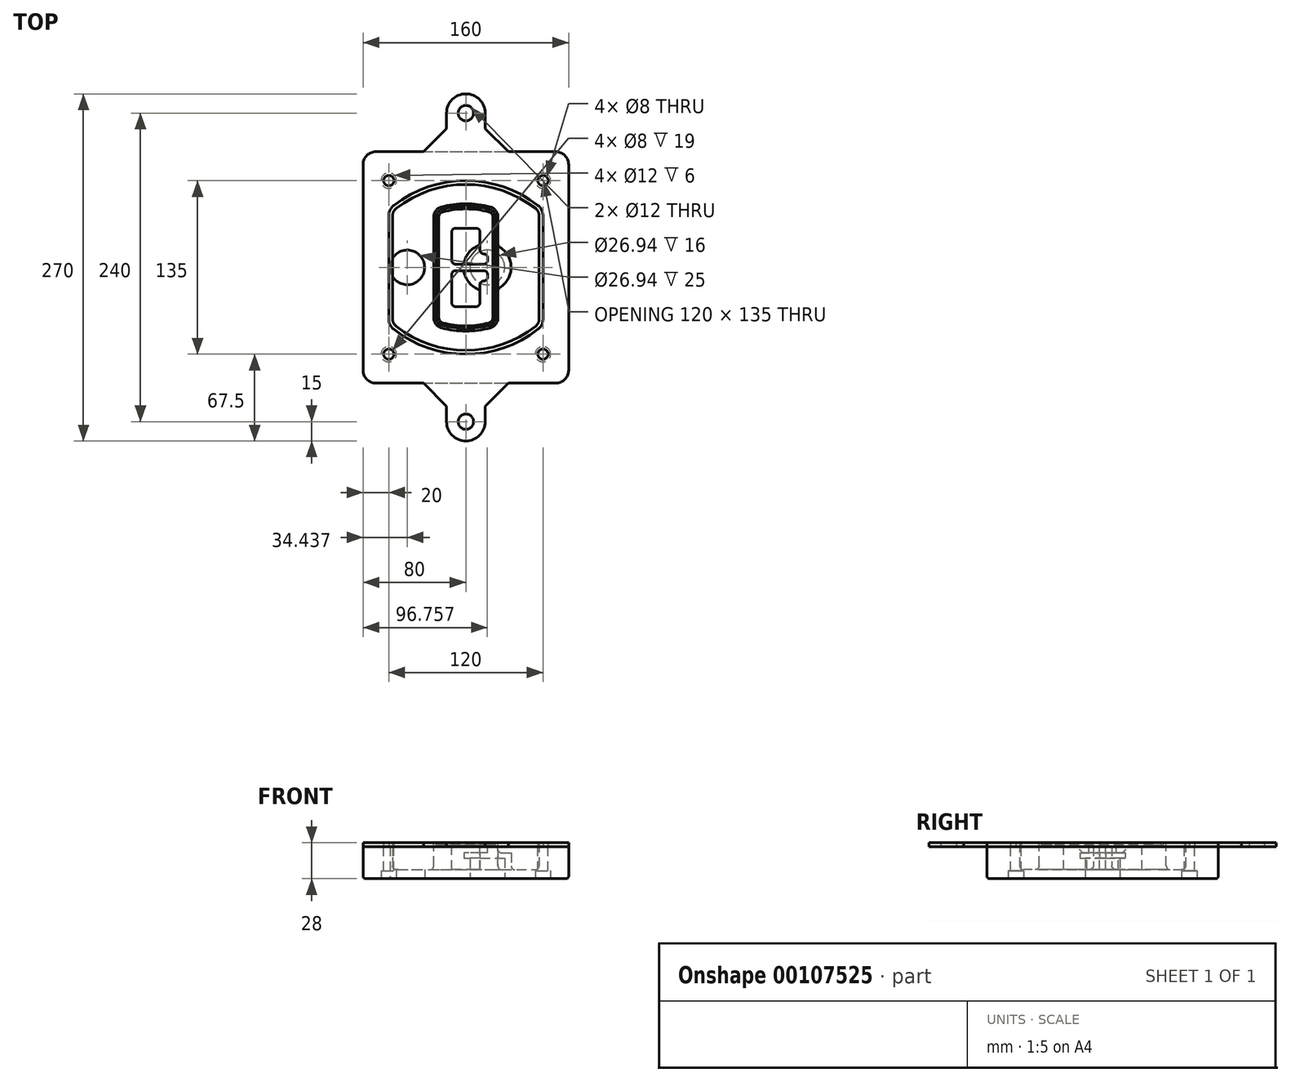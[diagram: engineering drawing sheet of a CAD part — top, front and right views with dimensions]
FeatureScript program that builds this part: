
annotation { "Feature Type Name" : "Feature", "Feature Type Description" : "" }
export const myFeature = defineFeature(function(context is Context, id is Id, definition is map)
    precondition{}
    {
        {
            var Q0;
            Q0=qCreatedBy(makeId("Top.planeOp"),FACE);
            var sketch = newSketch(context, id + "F0", { "sketchPlane" : qUnion([Q0])});
            skPoint(sketch, "E0.rect.middle", {"position": v(0, 0) * mm});
            skLineSegment(sketch, "E1.bottom", {"start": v(-70, -90) * mm, "end": v(70, -90) * mm});
            skLineSegment(sketch, "E1.top", {"start": v(-70, 90) * mm, "end": v(70, 90) * mm});
            skLineSegment(sketch, "E1.left", {"start": v(-80, -80) * mm, "end": v(-80, 80) * mm});
            skLineSegment(sketch, "E1.right", {"start": v(80, -80) * mm, "end": v(80, 80) * mm});
            skLineSegment(sketch, "E2", {"start": v(-80, 90) * mm, "end": v(80, -90) * mm, "construction": true});
            skLineSegment(sketch, "E3", {"start": v(80, 90) * mm, "end": v(-80, -90) * mm, "construction": true});
            skCircle(sketch, "E4", {"center": v(-60, 67.5) * mm, "radius": 4 * mm});
            skCircle(sketch, "E5", {"center": v(60, 67.5) * mm, "radius": 4 * mm});
            skCircle(sketch, "E6", {"center": v(60, -67.5) * mm, "radius": 4 * mm});
            skCircle(sketch, "E7", {"center": v(-60, -67.5) * mm, "radius": 4 * mm});
            skLineSegment(sketch, "E8", {"start": v(-60, 67.5) * mm, "end": v(60, 67.5) * mm, "construction": true});
            skLineSegment(sketch, "E9", {"start": v(60, 67.5) * mm, "end": v(60, -67.5) * mm, "construction": true});
            skLineSegment(sketch, "E10", {"start": v(60, -67.5) * mm, "end": v(-60, -67.5) * mm, "construction": true});
            skLineSegment(sketch, "E11", {"start": v(-60, -67.5) * mm, "end": v(-60, 67.5) * mm, "construction": true});
            skLineSegment(sketch, "E12", {"start": v(-60, 40.3) * mm, "end": v(-60, -40.3) * mm});
            skLineSegment(sketch, "E13", {"start": v(60, 40.3) * mm, "end": v(60, -40.3) * mm});
            skArc(sketch, "E14", {"start": v(56.15, 48.18) * mm, "mid": v(0, 67.5) * mm, "end": v(-56.15, 48.18) * mm});
            skArc(sketch, "E15", {"start": v(-56.15, -48.18) * mm, "mid": v(0, -67.5) * mm, "end": v(56.15, -48.18) * mm});
            skLineSegment(sketch, "E16", {"start": v(-60, 0) * mm, "end": v(60, 0) * mm, "construction": true});
            skPoint(sketch, "E17.visualSharp", {"position": v(-60, -45) * mm});
            skArc(sketch, "E17.filletArc", {"start": v(-60, -40.3) * mm, "mid": v(-58.99, -44.68) * mm, "end": v(-56.15, -48.18) * mm});
            skPoint(sketch, "E18.visualSharp", {"position": v(-60, 45) * mm});
            skArc(sketch, "E18.filletArc", {"start": v(-56.15, 48.18) * mm, "mid": v(-58.99, 44.68) * mm, "end": v(-60, 40.3) * mm});
            skPoint(sketch, "E19.visualSharp", {"position": v(60, 45) * mm});
            skArc(sketch, "E19.filletArc", {"start": v(60, 40.3) * mm, "mid": v(58.99, 44.68) * mm, "end": v(56.15, 48.18) * mm});
            skPoint(sketch, "E20.visualSharp", {"position": v(60, -45) * mm});
            skArc(sketch, "E20.filletArc", {"start": v(56.15, -48.18) * mm, "mid": v(58.99, -44.68) * mm, "end": v(60, -40.3) * mm});
            skPoint(sketch, "E21.visualSharp", {"position": v(-80, 90) * mm});
            skArc(sketch, "E21.filletArc", {"start": v(-70, 90) * mm, "mid": v(-77.07, 87.07) * mm, "end": v(-80, 80) * mm});
            skPoint(sketch, "E22.visualSharp", {"position": v(80, 90) * mm});
            skArc(sketch, "E22.filletArc", {"start": v(80, 80) * mm, "mid": v(77.07, 87.07) * mm, "end": v(70, 90) * mm});
            skPoint(sketch, "E23.visualSharp", {"position": v(80, -90) * mm});
            skArc(sketch, "E23.filletArc", {"start": v(70, -90) * mm, "mid": v(77.07, -87.07) * mm, "end": v(80, -80) * mm});
            skPoint(sketch, "E24.visualSharp", {"position": v(-80, -90) * mm});
            skArc(sketch, "E24.filletArc", {"start": v(-80, -80) * mm, "mid": v(-77.07, -87.07) * mm, "end": v(-70, -90) * mm});
            skArc(sketch, "E25.0", {"start": v(57, 40.3) * mm, "mid": v(56.3, 43.36) * mm, "end": v(54.3, 45.81) * mm});
            skLineSegment(sketch, "E25.1", {"start": v(57, 40.3) * mm, "end": v(57, -40.3) * mm});
            skArc(sketch, "E25.2", {"start": v(54.3, -45.81) * mm, "mid": v(56.3, -43.36) * mm, "end": v(57, -40.3) * mm});
            skArc(sketch, "E25.3", {"start": v(-54.3, -45.81) * mm, "mid": v(0, -64.5) * mm, "end": v(54.3, -45.81) * mm});
            skArc(sketch, "E25.4", {"start": v(-57, -40.3) * mm, "mid": v(-56.3, -43.36) * mm, "end": v(-54.3, -45.81) * mm});
            skArc(sketch, "E25.5", {"start": v(54.3, 45.81) * mm, "mid": v(0, 64.5) * mm, "end": v(-54.3, 45.81) * mm});
            skLineSegment(sketch, "E25.6", {"start": v(-57, 40.3) * mm, "end": v(-57, -40.3) * mm});
            skArc(sketch, "E25.7", {"start": v(-54.3, 45.81) * mm, "mid": v(-56.3, 43.36) * mm, "end": v(-57, 40.3) * mm});
            skArc(sketch, "E26.0", {"start": v(-58.62, 51.33) * mm, "mid": v(-62.58, 46.43) * mm, "end": v(-64, 40.3) * mm});
            skArc(sketch, "E26.1", {"start": v(58.62, 51.33) * mm, "mid": v(0, 71.5) * mm, "end": v(-58.62, 51.33) * mm});
            skArc(sketch, "E26.2", {"start": v(64, 40.3) * mm, "mid": v(62.58, 46.43) * mm, "end": v(58.62, 51.33) * mm});
            skLineSegment(sketch, "E26.3", {"start": v(64, 40.3) * mm, "end": v(64, -40.3) * mm});
            skArc(sketch, "E26.4", {"start": v(58.62, -51.33) * mm, "mid": v(62.58, -46.43) * mm, "end": v(64, -40.3) * mm});
            skLineSegment(sketch, "E26.5", {"start": v(-64, 40.3) * mm, "end": v(-64, -40.3) * mm});
            skArc(sketch, "E26.6", {"start": v(-58.62, -51.33) * mm, "mid": v(0, -71.5) * mm, "end": v(58.62, -51.33) * mm});
            skArc(sketch, "E26.7", {"start": v(-64, -40.3) * mm, "mid": v(-62.58, -46.43) * mm, "end": v(-58.62, -51.33) * mm});
            skSolve(sketch);
        }
        {
            var Q0;
            Q0=makeQuery(id+"F0.imprint","IMPRINT",FACE,{"disambiguationData":[TD([[makeQuery(id+"F0.imprint","IMPRINT",EDGE,{"derivedFrom":sQuery(id+"F0.wireOp",EDGE,"E1.bottom")}),1.0]])]});
            var Q1;
            Q1=makeQuery(id+"F0.imprint","IMPRINT",FACE,{"disambiguationData":[TD([[makeQuery(id+"F0.imprint","IMPRINT",EDGE,{"derivedFrom":sQuery(id+"F0.wireOp",EDGE,"E12")}),1.0]])]});
            var Q2;
            Q2=makeQuery(id+"F0.imprint","IMPRINT",FACE,{"disambiguationData":[TD([[makeQuery(id+"F0.imprint","IMPRINT",EDGE,{"derivedFrom":sQuery(id+"F0.wireOp",EDGE,"E25.0")}),1.0]])]});
            var Q3;
            Q3=makeQuery(id+"F0.imprint","IMPRINT",FACE,{"disambiguationData":[TD([[makeQuery(id+"F0.imprint","IMPRINT",EDGE,{"derivedFrom":sQuery(id+"F0.wireOp",EDGE,"E12")}),-1.0]])]});
            extrude(context, id + "F1", {"entities" : qUnion([Q0, Q1, Q2, Q3]), "oppositeDirection" : true, "depth" : 25 * mm});
        }
        {
            var Q0;
            Q0=makeQuery(id+"F0.imprint","IMPRINT",FACE,{"disambiguationData":[TD([[makeQuery(id+"F0.imprint","IMPRINT",EDGE,{"derivedFrom":sQuery(id+"F0.wireOp",EDGE,"E12")}),1.0]])]});
            extrude(context, id + "F2", {"entities" : qUnion([Q0]), "operationType" : NewBodyOperationType.ADD, "depth" : 3 * mm});
        }
        {
            var Q0;
            Q0=makeQuery(id+"F0.imprint","IMPRINT",FACE,{"disambiguationData":[TD([[makeQuery(id+"F0.imprint","IMPRINT",EDGE,{"derivedFrom":sQuery(id+"F0.wireOp",EDGE,"E25.0")}),1.0]])]});
            extrude(context, id + "F3", {"entities" : qUnion([Q0]), "operationType" : NewBodyOperationType.REMOVE, "oppositeDirection" : true, "depth" : 18 * mm});
        }
        {
            var Q0;
            Q0=makeQuery(id+"F2.opExtrude","CAP_FACE",FACE,{"disambiguationData":[OSD([sQuery(id+"F0.wireOp",EDGE,"E12"),sQuery(id+"F0.wireOp",EDGE,"E13"),sQuery(id+"F0.wireOp",EDGE,"E14"),sQuery(id+"F0.wireOp",EDGE,"E15"),sQuery(id+"F0.wireOp",EDGE,"E17.filletArc"),sQuery(id+"F0.wireOp",EDGE,"E18.filletArc"),sQuery(id+"F0.wireOp",EDGE,"E19.filletArc"),sQuery(id+"F0.wireOp",EDGE,"E20.filletArc"),sQuery(id+"F0.wireOp",EDGE,"E25.0"),sQuery(id+"F0.wireOp",EDGE,"E25.1"),sQuery(id+"F0.wireOp",EDGE,"E25.2"),sQuery(id+"F0.wireOp",EDGE,"E25.3"),sQuery(id+"F0.wireOp",EDGE,"E25.4"),sQuery(id+"F0.wireOp",EDGE,"E25.5"),sQuery(id+"F0.wireOp",EDGE,"E25.6"),sQuery(id+"F0.wireOp",EDGE,"E25.7")])],"isStart":false});
            var sketch = newSketch(context, id + "F4", { "sketchPlane" : qUnion([Q0])});
            skArc(sketch, "E27.0", {"start": v(-19.08, -46.97) * mm, "mid": v(0, -49.5) * mm, "end": v(19.08, -46.97) * mm});
            skArc(sketch, "E28.0", {"start": v(19.08, 46.97) * mm, "mid": v(0, 49.5) * mm, "end": v(-19.08, 46.97) * mm});
            skLineSegment(sketch, "E29", {"start": v(-25, 39.25) * mm, "end": v(-25, -39.25) * mm});
            skLineSegment(sketch, "E30", {"start": v(25, 39.25) * mm, "end": v(25, -39.25) * mm});
            skLineSegment(sketch, "E31", {"start": v(-25, 45.1) * mm, "end": v(25, 45.1) * mm, "construction": true});
            skLineSegment(sketch, "E32", {"start": v(-25, -45.1) * mm, "end": v(25, -45.1) * mm, "construction": true});
            skPoint(sketch, "E33.visualSharp", {"position": v(-25, 45.1) * mm});
            skArc(sketch, "E33.filletArc", {"start": v(-19.08, 46.97) * mm, "mid": v(-23.35, 44.11) * mm, "end": v(-25, 39.25) * mm});
            skPoint(sketch, "E34.visualSharp", {"position": v(25, 45.1) * mm});
            skArc(sketch, "E34.filletArc", {"start": v(25, 39.25) * mm, "mid": v(23.35, 44.11) * mm, "end": v(19.08, 46.97) * mm});
            skPoint(sketch, "E35.visualSharp", {"position": v(25, -45.1) * mm});
            skArc(sketch, "E35.filletArc", {"start": v(19.08, -46.97) * mm, "mid": v(23.35, -44.11) * mm, "end": v(25, -39.25) * mm});
            skPoint(sketch, "E36.visualSharp", {"position": v(-25, -45.1) * mm});
            skArc(sketch, "E36.filletArc", {"start": v(-25, -39.25) * mm, "mid": v(-23.35, -44.11) * mm, "end": v(-19.08, -46.97) * mm});
            skArc(sketch, "E37.0", {"start": v(54.3, 45.81) * mm, "mid": v(0, 64.5) * mm, "end": v(-54.3, 45.81) * mm});
            skArc(sketch, "E37.1", {"start": v(-54.3, 45.81) * mm, "mid": v(-56.3, 43.36) * mm, "end": v(-57, 40.3) * mm});
            skLineSegment(sketch, "E37.2", {"start": v(-57, 40.3) * mm, "end": v(-57, -40.3) * mm});
            skArc(sketch, "E37.3", {"start": v(-57, -40.3) * mm, "mid": v(-56.3, -43.36) * mm, "end": v(-54.3, -45.81) * mm});
            skArc(sketch, "E37.4", {"start": v(-54.3, -45.81) * mm, "mid": v(0, -64.5) * mm, "end": v(54.3, -45.81) * mm});
            skArc(sketch, "E37.5", {"start": v(54.3, -45.81) * mm, "mid": v(56.3, -43.36) * mm, "end": v(57, -40.3) * mm});
            skLineSegment(sketch, "E37.6", {"start": v(57, 40.3) * mm, "end": v(57, -40.3) * mm});
            skArc(sketch, "E37.7", {"start": v(57, 40.3) * mm, "mid": v(56.3, 43.36) * mm, "end": v(54.3, 45.81) * mm});
            skLineSegment(sketch, "E38.0", {"start": v(23, 39.25) * mm, "end": v(23, -39.25) * mm});
            skArc(sketch, "E38.1", {"start": v(18.56, -45.04) * mm, "mid": v(21.76, -42.9) * mm, "end": v(23, -39.25) * mm});
            skArc(sketch, "E38.2", {"start": v(-18.56, -45.04) * mm, "mid": v(0, -47.5) * mm, "end": v(18.56, -45.04) * mm});
            skArc(sketch, "E38.3", {"start": v(-23, -39.25) * mm, "mid": v(-21.76, -42.9) * mm, "end": v(-18.56, -45.04) * mm});
            skLineSegment(sketch, "E38.4", {"start": v(-23, 39.25) * mm, "end": v(-23, -39.25) * mm});
            skArc(sketch, "E38.5", {"start": v(23, 39.25) * mm, "mid": v(21.76, 42.9) * mm, "end": v(18.56, 45.04) * mm});
            skArc(sketch, "E38.6", {"start": v(-18.56, 45.04) * mm, "mid": v(-21.76, 42.9) * mm, "end": v(-23, 39.25) * mm});
            skArc(sketch, "E38.7", {"start": v(18.56, 45.04) * mm, "mid": v(0, 47.5) * mm, "end": v(-18.56, 45.04) * mm});
            skArc(sketch, "E39.0", {"start": v(21, 39.25) * mm, "mid": v(20.18, 41.68) * mm, "end": v(18.04, 43.1) * mm});
            skLineSegment(sketch, "E39.1", {"start": v(21, 39.25) * mm, "end": v(21, -39.25) * mm});
            skArc(sketch, "E39.2", {"start": v(18.04, -43.1) * mm, "mid": v(20.18, -41.68) * mm, "end": v(21, -39.25) * mm});
            skArc(sketch, "E39.3", {"start": v(-18.04, -43.1) * mm, "mid": v(0, -45.5) * mm, "end": v(18.04, -43.1) * mm});
            skArc(sketch, "E39.4", {"start": v(-21, -39.25) * mm, "mid": v(-20.18, -41.68) * mm, "end": v(-18.04, -43.1) * mm});
            skArc(sketch, "E39.5", {"start": v(18.04, 43.1) * mm, "mid": v(0, 45.5) * mm, "end": v(-18.04, 43.1) * mm});
            skLineSegment(sketch, "E39.6", {"start": v(-21, 39.25) * mm, "end": v(-21, -39.25) * mm});
            skArc(sketch, "E39.7", {"start": v(-18.04, 43.1) * mm, "mid": v(-20.18, 41.68) * mm, "end": v(-21, 39.25) * mm});
            skLineSegment(sketch, "E40", {"start": v(-25, 0) * mm, "end": v(25, 0) * mm, "construction": true});
            skLineSegment(sketch, "E41", {"start": v(-11, 5.5) * mm, "end": v(-11, 27.5) * mm});
            skLineSegment(sketch, "E42", {"start": v(-8, 30.5) * mm, "end": v(8, 30.5) * mm});
            skLineSegment(sketch, "E43", {"start": v(11, 27.5) * mm, "end": v(11, 13.5) * mm});
            skLineSegment(sketch, "E44", {"start": v(14, 10.5) * mm, "end": v(14, 10.5) * mm});
            skLineSegment(sketch, "E45", {"start": v(17, 7.5) * mm, "end": v(17, 5.5) * mm});
            skLineSegment(sketch, "E46", {"start": v(14, 2.5) * mm, "end": v(-8, 2.5) * mm});
            skPoint(sketch, "E47.visualSharp", {"position": v(-11, 30.5) * mm});
            skArc(sketch, "E47.filletArc", {"start": v(-8, 30.5) * mm, "mid": v(-10.12, 29.62) * mm, "end": v(-11, 27.5) * mm});
            skPoint(sketch, "E48.visualSharp", {"position": v(11, 30.5) * mm});
            skArc(sketch, "E48.filletArc", {"start": v(11, 27.5) * mm, "mid": v(10.12, 29.62) * mm, "end": v(8, 30.5) * mm});
            skPoint(sketch, "E49.visualSharp", {"position": v(11, 10.5) * mm});
            skArc(sketch, "E49.filletArc", {"start": v(11, 13.5) * mm, "mid": v(11.88, 11.38) * mm, "end": v(14, 10.5) * mm});
            skPoint(sketch, "E50.visualSharp", {"position": v(17, 10.5) * mm});
            skArc(sketch, "E50.filletArc", {"start": v(17, 7.5) * mm, "mid": v(16.12, 9.62) * mm, "end": v(14, 10.5) * mm});
            skPoint(sketch, "E51.visualSharp", {"position": v(17, 2.5) * mm});
            skArc(sketch, "E51.filletArc", {"start": v(14, 2.5) * mm, "mid": v(16.12, 3.38) * mm, "end": v(17, 5.5) * mm});
            skPoint(sketch, "E52.visualSharp", {"position": v(-11, 2.5) * mm});
            skArc(sketch, "E52.filletArc", {"start": v(-11, 5.5) * mm, "mid": v(-10.12, 3.38) * mm, "end": v(-8, 2.5) * mm});
            skLineSegment(sketch, "E53.0.MirrorCS", {"start": v(14, -2.5) * mm, "end": v(-8, -2.5) * mm});
            skArc(sketch, "E54.0.MirrorCS", {"start": v(-11, -5.5) * mm, "mid": v(-10.12, -3.38) * mm, "end": v(-8, -2.5) * mm});
            skLineSegment(sketch, "E55.0.MirrorCS", {"start": v(-11, -5.5) * mm, "end": v(-11, -27.5) * mm});
            skArc(sketch, "E56.0.MirrorCS", {"start": v(-8, -30.5) * mm, "mid": v(-10.12, -29.62) * mm, "end": v(-11, -27.5) * mm});
            skLineSegment(sketch, "E57.0.MirrorCS", {"start": v(-8, -30.5) * mm, "end": v(8, -30.5) * mm});
            skArc(sketch, "E58.0.MirrorCS", {"start": v(11, -27.5) * mm, "mid": v(10.12, -29.62) * mm, "end": v(8, -30.5) * mm});
            skLineSegment(sketch, "E59.0.MirrorCS", {"start": v(11, -27.5) * mm, "end": v(11, -13.5) * mm});
            skArc(sketch, "E60.0.MirrorCS", {"start": v(11, -13.5) * mm, "mid": v(11.88, -11.38) * mm, "end": v(14, -10.5) * mm});
            skArc(sketch, "E61.0.MirrorCS", {"start": v(17, -7.5) * mm, "mid": v(16.12, -9.62) * mm, "end": v(14, -10.5) * mm});
            skLineSegment(sketch, "E62.0.MirrorCS", {"start": v(17, -7.5) * mm, "end": v(17, -5.5) * mm});
            skArc(sketch, "E63.0.MirrorCS", {"start": v(14, -2.5) * mm, "mid": v(16.12, -3.38) * mm, "end": v(17, -5.5) * mm});
            skSolve(sketch);
        }
        {
            var Q0;
            Q0=makeQuery(id+"F4.imprint","IMPRINT",FACE,{"disambiguationData":[TD([[makeQuery(id+"F4.imprint","IMPRINT",EDGE,{"derivedFrom":sQuery(id+"F4.wireOp",EDGE,"E27.0")}),1.0]])]});
            var Q1;
            Q1=makeQuery(id+"F4.imprint","IMPRINT",FACE,{"disambiguationData":[TD([[makeQuery(id+"F4.imprint","IMPRINT",EDGE,{"derivedFrom":sQuery(id+"F4.wireOp",EDGE,"E38.0")}),-1.0]])]});
            var Q2;
            Q2=makeQuery(id+"F4.imprint","IMPRINT",FACE,{"disambiguationData":[TD([[makeQuery(id+"F4.imprint","IMPRINT",EDGE,{"derivedFrom":sQuery(id+"F4.wireOp",EDGE,"E39.0")}),1.0]])]});
            extrude(context, id + "F5", {"entities" : qUnion([Q0, Q1, Q2]), "operationType" : NewBodyOperationType.ADD, "endBound" : BoundingType.UP_TO_NEXT, "oppositeDirection" : true, "depth" : 25 * mm});
        }
        {
            var Q0;
            Q0=makeQuery(id+"F4.imprint","IMPRINT",FACE,{"disambiguationData":[TD([[makeQuery(id+"F4.imprint","IMPRINT",EDGE,{"derivedFrom":sQuery(id+"F4.wireOp",EDGE,"E38.0")}),-1.0]])]});
            extrude(context, id + "F6", {"entities" : qUnion([Q0]), "operationType" : NewBodyOperationType.REMOVE, "oppositeDirection" : true, "depth" : 2 * mm});
        }
        {
            var Q0;
            Q0=makeQuery(id+"F1.opExtrude","CAP_FACE",FACE,{"disambiguationData":[OSD([sQuery(id+"F0.wireOp",EDGE,"E1.bottom"),sQuery(id+"F0.wireOp",EDGE,"E1.top"),sQuery(id+"F0.wireOp",EDGE,"E1.left"),sQuery(id+"F0.wireOp",EDGE,"E1.right"),sQuery(id+"F0.wireOp",EDGE,"E4"),sQuery(id+"F0.wireOp",EDGE,"E5"),sQuery(id+"F0.wireOp",EDGE,"E6"),sQuery(id+"F0.wireOp",EDGE,"E7"),sQuery(id+"F0.wireOp",EDGE,"E21.filletArc"),sQuery(id+"F0.wireOp",EDGE,"E22.filletArc"),sQuery(id+"F0.wireOp",EDGE,"E23.filletArc"),sQuery(id+"F0.wireOp",EDGE,"E24.filletArc")])],"isStart":false});
            var sketch = newSketch(context, id + "F7", { "sketchPlane" : qUnion([Q0])});
            skCircle(sketch, "E64", {"center": v(16.76, 0) * mm, "radius": 13.47 * mm});
            skCircle(sketch, "E65", {"center": v(-45.56, 0) * mm, "radius": 13.47 * mm});
            skLineSegment(sketch, "E66", {"start": v(80, 0) * mm, "end": v(-80, 0) * mm});
            skCircle(sketch, "E67", {"center": v(16.76, 0) * mm, "radius": 18.47 * mm});
            skCircle(sketch, "E68", {"center": v(60, -67.5) * mm, "radius": 6 * mm});
            skCircle(sketch, "E69", {"center": v(-60, -67.5) * mm, "radius": 6 * mm});
            skCircle(sketch, "E70", {"center": v(-60, 67.5) * mm, "radius": 6 * mm});
            skCircle(sketch, "E71", {"center": v(60, 67.5) * mm, "radius": 6 * mm});
            skSolve(sketch);
        }
        {
            var Q0;
            {var subQ1=sQuery(id+"F7.wireOp",EDGE,"E66");var subQ4=sQuery(id+"F7.wireOp",EDGE,"E64");var subQ6=makeQuery(id+"F7.imprint","INTERSECT",VERTEX,{"disambiguationData":[OD(0.0)],"derivedFrom":[subQ4,subQ1]});Q0=makeQuery(id+"F7.imprint","IMPRINT",FACE,{"disambiguationData":[TD([[makeQuery(id+"F7.imprint","IMPRINT",EDGE,{"disambiguationData":[TD([[subQ6,-1.0]])],"derivedFrom":subQ4}),-1.0]])]});}
            var Q1;
            {var subQ0=sQuery(id+"F7.wireOp",EDGE,"E66");var subQ1=sQuery(id+"F7.wireOp",EDGE,"E64");var subQ3=makeQuery(id+"F7.imprint","INTERSECT",VERTEX,{"disambiguationData":[OD(0.0)],"derivedFrom":[subQ1,subQ0]});Q1=makeQuery(id+"F7.imprint","IMPRINT",FACE,{"disambiguationData":[TD([[makeQuery(id+"F7.imprint","IMPRINT",EDGE,{"disambiguationData":[TD([[subQ3,-1.0]])],"derivedFrom":subQ1}),1.0]])]});}
            var Q2;
            {var subQ0=sQuery(id+"F7.wireOp",EDGE,"E66");var subQ1=sQuery(id+"F7.wireOp",EDGE,"E64");var subQ3=makeQuery(id+"F7.imprint","INTERSECT",VERTEX,{"disambiguationData":[OD(0.0)],"derivedFrom":[subQ1,subQ0]});Q2=makeQuery(id+"F7.imprint","IMPRINT",FACE,{"disambiguationData":[TD([[makeQuery(id+"F7.imprint","IMPRINT",EDGE,{"disambiguationData":[TD([[subQ3,1.0]])],"derivedFrom":subQ1}),1.0]])]});}
            var Q3;
            {var subQ1=sQuery(id+"F7.wireOp",EDGE,"E66");var subQ4=sQuery(id+"F7.wireOp",EDGE,"E64");var subQ6=makeQuery(id+"F7.imprint","INTERSECT",VERTEX,{"disambiguationData":[OD(0.0)],"derivedFrom":[subQ4,subQ1]});Q3=makeQuery(id+"F7.imprint","IMPRINT",FACE,{"disambiguationData":[TD([[makeQuery(id+"F7.imprint","IMPRINT",EDGE,{"disambiguationData":[TD([[subQ6,1.0]])],"derivedFrom":subQ4}),-1.0]])]});}
            extrude(context, id + "F8", {"entities" : qUnion([Q0, Q1, Q2, Q3]), "operationType" : NewBodyOperationType.ADD, "oppositeDirection" : true, "depth" : 20 * mm});
        }
        {
            var Q0;
            {var subQ0=sQuery(id+"F7.wireOp",EDGE,"E66");var subQ1=sQuery(id+"F7.wireOp",EDGE,"E64");var subQ3=makeQuery(id+"F7.imprint","INTERSECT",VERTEX,{"disambiguationData":[OD(0.0)],"derivedFrom":[subQ1,subQ0]});Q0=makeQuery(id+"F7.imprint","IMPRINT",FACE,{"disambiguationData":[TD([[makeQuery(id+"F7.imprint","IMPRINT",EDGE,{"disambiguationData":[TD([[subQ3,-1.0]])],"derivedFrom":subQ1}),1.0]])]});}
            var Q1;
            {var subQ0=sQuery(id+"F7.wireOp",EDGE,"E66");var subQ1=sQuery(id+"F7.wireOp",EDGE,"E64");var subQ3=makeQuery(id+"F7.imprint","INTERSECT",VERTEX,{"disambiguationData":[OD(0.0)],"derivedFrom":[subQ1,subQ0]});Q1=makeQuery(id+"F7.imprint","IMPRINT",FACE,{"disambiguationData":[TD([[makeQuery(id+"F7.imprint","IMPRINT",EDGE,{"disambiguationData":[TD([[subQ3,1.0]])],"derivedFrom":subQ1}),1.0]])]});}
            extrude(context, id + "F9", {"entities" : qUnion([Q0, Q1]), "operationType" : NewBodyOperationType.REMOVE, "oppositeDirection" : true, "depth" : 16 * mm});
        }
        {
            var Q0;
            {var subQ0=sQuery(id+"F7.wireOp",EDGE,"E66");var subQ1=sQuery(id+"F7.wireOp",EDGE,"E65");var subQ3=makeQuery(id+"F7.imprint","INTERSECT",VERTEX,{"disambiguationData":[OD(0.0)],"derivedFrom":[subQ1,subQ0]});Q0=makeQuery(id+"F7.imprint","IMPRINT",FACE,{"disambiguationData":[TD([[makeQuery(id+"F7.imprint","IMPRINT",EDGE,{"disambiguationData":[TD([[subQ3,-1.0]])],"derivedFrom":subQ1}),1.0]])]});}
            var Q1;
            {var subQ0=sQuery(id+"F7.wireOp",EDGE,"E66");var subQ1=sQuery(id+"F7.wireOp",EDGE,"E65");var subQ3=makeQuery(id+"F7.imprint","INTERSECT",VERTEX,{"disambiguationData":[OD(0.0)],"derivedFrom":[subQ1,subQ0]});Q1=makeQuery(id+"F7.imprint","IMPRINT",FACE,{"disambiguationData":[TD([[makeQuery(id+"F7.imprint","IMPRINT",EDGE,{"disambiguationData":[TD([[subQ3,1.0]])],"derivedFrom":subQ1}),1.0]])]});}
            extrude(context, id + "F10", {"entities" : qUnion([Q0, Q1]), "operationType" : NewBodyOperationType.REMOVE, "oppositeDirection" : true, "depth" : 25 * mm});
        }
        {
            var Q0;
            Q0=makeQuery(id+"F7.imprint","IMPRINT",FACE,{"disambiguationData":[TD([[makeQuery(id+"F7.imprint","IMPRINT",EDGE,{"derivedFrom":sQuery(id+"F7.wireOp",EDGE,"E68")}),1.0]])]});
            var Q1;
            Q1=makeQuery(id+"F7.imprint","IMPRINT",FACE,{"disambiguationData":[TD([[makeQuery(id+"F7.imprint","IMPRINT",EDGE,{"derivedFrom":makeQuery(id+"F1.opExtrude","CAP_EDGE",EDGE,{"disambiguationData":[OSD([sQuery(id+"F0.wireOp",EDGE,"E5")])],"isStart":false})}),-1.0]])]});
            var Q2;
            Q2=makeQuery(id+"F7.imprint","IMPRINT",FACE,{"disambiguationData":[TD([[makeQuery(id+"F7.imprint","IMPRINT",EDGE,{"derivedFrom":sQuery(id+"F7.wireOp",EDGE,"E69")}),1.0]])]});
            var Q3;
            Q3=makeQuery(id+"F7.imprint","IMPRINT",FACE,{"disambiguationData":[TD([[makeQuery(id+"F7.imprint","IMPRINT",EDGE,{"derivedFrom":makeQuery(id+"F1.opExtrude","CAP_EDGE",EDGE,{"disambiguationData":[OSD([sQuery(id+"F0.wireOp",EDGE,"E4")])],"isStart":false})}),-1.0]])]});
            var Q4;
            Q4=makeQuery(id+"F7.imprint","IMPRINT",FACE,{"disambiguationData":[TD([[makeQuery(id+"F7.imprint","IMPRINT",EDGE,{"derivedFrom":sQuery(id+"F7.wireOp",EDGE,"E70")}),1.0]])]});
            var Q5;
            Q5=makeQuery(id+"F7.imprint","IMPRINT",FACE,{"disambiguationData":[TD([[makeQuery(id+"F7.imprint","IMPRINT",EDGE,{"derivedFrom":makeQuery(id+"F1.opExtrude","CAP_EDGE",EDGE,{"disambiguationData":[OSD([sQuery(id+"F0.wireOp",EDGE,"E7")])],"isStart":false})}),-1.0]])]});
            var Q6;
            Q6=makeQuery(id+"F7.imprint","IMPRINT",FACE,{"disambiguationData":[TD([[makeQuery(id+"F7.imprint","IMPRINT",EDGE,{"derivedFrom":sQuery(id+"F7.wireOp",EDGE,"E71")}),1.0]])]});
            var Q7;
            Q7=makeQuery(id+"F7.imprint","IMPRINT",FACE,{"disambiguationData":[TD([[makeQuery(id+"F7.imprint","IMPRINT",EDGE,{"derivedFrom":makeQuery(id+"F1.opExtrude","CAP_EDGE",EDGE,{"disambiguationData":[OSD([sQuery(id+"F0.wireOp",EDGE,"E6")])],"isStart":false})}),-1.0]])]});
            extrude(context, id + "F11", {"entities" : qUnion([Q0, Q1, Q2, Q3, Q4, Q5, Q6, Q7]), "operationType" : NewBodyOperationType.REMOVE, "oppositeDirection" : true, "depth" : 6 * mm});
        }
        {
            var Q0;
            Q0=makeQuery(id+"F9.boolean.opBoolean","COPY",FACE,{"derivedFrom":makeQuery(id+"F9.opExtrude","CAP_FACE",FACE,{"disambiguationData":[OSD([sQuery(id+"F7.wireOp",EDGE,"E64")])],"isStart":false})});
            var sketch = newSketch(context, id + "F12", { "sketchPlane" : qUnion([Q0])});
            skArc(sketch, "E72.0", {"start": v(11, 17.55) * mm, "mid": v(2.57, 11.82) * mm, "end": v(-1.54, 2.5) * mm});
            skArc(sketch, "E72.1", {"start": v(-1.54, -2.5) * mm, "mid": v(2.57, -11.82) * mm, "end": v(11, -17.55) * mm});
            skLineSegment(sketch, "E73", {"start": v(-1.54, -2.5) * mm, "end": v(14, -2.5) * mm});
            skLineSegment(sketch, "E74.0", {"start": v(14, 2.5) * mm, "end": v(-1.54, 2.5) * mm});
            skArc(sketch, "E74.1", {"start": v(14, 2.5) * mm, "mid": v(16.12, 3.38) * mm, "end": v(17, 5.5) * mm});
            skLineSegment(sketch, "E74.2", {"start": v(17, 7.5) * mm, "end": v(17, 5.5) * mm});
            skArc(sketch, "E74.3", {"start": v(17, 7.5) * mm, "mid": v(16.12, 9.62) * mm, "end": v(14, 10.5) * mm});
            skArc(sketch, "E74.4", {"start": v(11, 13.5) * mm, "mid": v(11.88, 11.38) * mm, "end": v(14, 10.5) * mm});
            skLineSegment(sketch, "E74.5", {"start": v(11, 17.55) * mm, "end": v(11, 13.5) * mm});
            skLineSegment(sketch, "E74.7", {"start": v(14, -2.5) * mm, "end": v(-1.54, -2.5) * mm});
            skArc(sketch, "E74.8", {"start": v(14, -2.5) * mm, "mid": v(16.12, -3.38) * mm, "end": v(17, -5.5) * mm});
            skLineSegment(sketch, "E74.9", {"start": v(17, -7.5) * mm, "end": v(17, -5.5) * mm});
            skArc(sketch, "E74.10", {"start": v(17, -7.5) * mm, "mid": v(16.12, -9.62) * mm, "end": v(14, -10.5) * mm});
            skArc(sketch, "E74.11", {"start": v(11, -13.5) * mm, "mid": v(11.88, -11.38) * mm, "end": v(14, -10.5) * mm});
            skLineSegment(sketch, "E74.12", {"start": v(11, -17.55) * mm, "end": v(11, -13.5) * mm});
            skPoint(sketch, "E75.orphan", {"position": v(11, -27.5) * mm});
            skPoint(sketch, "E76.orphan", {"position": v(-8, -2.5) * mm});
            skPoint(sketch, "E77.orphan", {"position": v(-8, 2.5) * mm});
            skPoint(sketch, "E78.orphan", {"position": v(11, 27.5) * mm});
            skSolve(sketch);
        }
        {
            var Q0;
            {var subQ7=sQuery(id+"F12.wireOp",EDGE,"E72.0");var subQ14=sQuery(id+"F12.wireOp",EDGE,"E72.1");var subQ16=sQuery(id+"F12.wireOp",EDGE,"E74.1");var subQ18=sQuery(id+"F12.wireOp",EDGE,"E74.8");Q0=qUnion([makeQuery(id+"F12.imprint","IMPRINT",FACE,{"disambiguationData":[TD([[makeQuery(id+"F12.imprint","IMPRINT",EDGE,{"derivedFrom":subQ7}),1.0]])]}),makeQuery(id+"F12.imprint","IMPRINT",FACE,{"disambiguationData":[TD([[makeQuery(id+"F12.imprint","IMPRINT",EDGE,{"derivedFrom":subQ14}),1.0]])]}),makeQuery(id+"F12.imprint","IMPRINT",FACE,{"disambiguationData":[TD([[makeQuery(id+"F12.imprint","IMPRINT",EDGE,{"derivedFrom":subQ16}),1.0]])]}),makeQuery(id+"F12.imprint","IMPRINT",FACE,{"disambiguationData":[TD([[makeQuery(id+"F12.imprint","IMPRINT",EDGE,{"derivedFrom":subQ18}),-1.0]])]})]);}
            var Q1;
            Q1=makeQuery(id+"F5.boolean.opBoolean","SPLIT",FACE,{"disambiguationData":[TD([makeQuery(id+"F5.opExtrude","SWEPT_FACE",FACE,{"disambiguationData":[OSD([sQuery(id+"F4.wireOp",EDGE,"E41")])]})])],"derivedFrom":makeQuery(id+"F3.boolean.opBoolean","COPY",FACE,{"derivedFrom":makeQuery(id+"F3.opExtrude","CAP_FACE",FACE,{"disambiguationData":[OSD([sQuery(id+"F0.wireOp",EDGE,"E25.0"),sQuery(id+"F0.wireOp",EDGE,"E25.1"),sQuery(id+"F0.wireOp",EDGE,"E25.2"),sQuery(id+"F0.wireOp",EDGE,"E25.3"),sQuery(id+"F0.wireOp",EDGE,"E25.4"),sQuery(id+"F0.wireOp",EDGE,"E25.5"),sQuery(id+"F0.wireOp",EDGE,"E25.6"),sQuery(id+"F0.wireOp",EDGE,"E25.7")])],"isStart":false})})});
            extrude(context, id + "F13", {"entities" : qUnion([Q0]), "operationType" : NewBodyOperationType.REMOVE, "endBound" : BoundingType.UP_TO_SURFACE, "endBoundEntityFace" : qUnion([Q1]), "depth" : 25 * mm});
        }
        {
            var Q0;
            Q0=makeQuery(id+"F3.boolean.opBoolean","COPY",EDGE,{"derivedFrom":makeQuery(id+"F3.opExtrude","CAP_EDGE",EDGE,{"disambiguationData":[OSD([sQuery(id+"F0.wireOp",EDGE,"E25.6")])],"isStart":false})});
            var Q1;
            Q1=makeQuery(id+"F8.boolean.opBoolean","INTERSECT",EDGE,{"derivedFrom":[makeQuery(id+"F5.opExtrude","SWEPT_FACE",FACE,{"disambiguationData":[OSD([sQuery(id+"F4.wireOp",EDGE,"E30")])]}),makeQuery(id+"F8.opExtrude","CAP_FACE",FACE,{"disambiguationData":[OSD([sQuery(id+"F7.wireOp",EDGE,"E67")])],"isStart":false})]});
            var Q2;
            Q2=makeQuery(id+"F8.boolean.opBoolean","INTERSECT",EDGE,{"disambiguationData":[OD(1.0)],"derivedFrom":[makeQuery(id+"F5.opExtrude","SWEPT_FACE",FACE,{"disambiguationData":[OSD([sQuery(id+"F4.wireOp",EDGE,"E30")])]}),makeQuery(id+"F8.opExtrude","SWEPT_FACE",FACE,{"disambiguationData":[OSD([sQuery(id+"F7.wireOp",EDGE,"E67")])]})]});
            var Q3;
            {var subQ0=sQuery(id+"F4.wireOp",EDGE,"E30");Q3=makeQuery(id+"F8.boolean.opBoolean","SPLIT",EDGE,{"disambiguationData":[TD([makeQuery(id+"F5.opExtrude","SWEPT_FACE",FACE,{"disambiguationData":[OSD([sQuery(id+"F4.wireOp",EDGE,"E35.filletArc")])]})])],"derivedFrom":makeQuery(id+"F5.opExtrude","CAP_EDGE",EDGE,{"disambiguationData":[OSD([subQ0])],"isStart":false})});}
            var Q4;
            {var subQ0=sQuery(id+"F0.wireOp",EDGE,"E25.7");var subQ1=sQuery(id+"F0.wireOp",EDGE,"E25.1");var subQ2=sQuery(id+"F0.wireOp",EDGE,"E25.6");var subQ3=sQuery(id+"F0.wireOp",EDGE,"E25.5");var subQ4=sQuery(id+"F0.wireOp",EDGE,"E25.4");var subQ5=sQuery(id+"F0.wireOp",EDGE,"E25.0");var subQ6=sQuery(id+"F0.wireOp",EDGE,"E25.2");var subQ7=sQuery(id+"F0.wireOp",EDGE,"E25.3");Q4=makeQuery(id+"F8.boolean.opBoolean","INTERSECT",EDGE,{"derivedFrom":[makeQuery(id+"F5.boolean.opBoolean","SPLIT",FACE,{"disambiguationData":[TD([makeQuery(id+"F2.opExtrude","SWEPT_FACE",FACE,{"disambiguationData":[OSD([subQ5])]})])],"derivedFrom":makeQuery(id+"F3.boolean.opBoolean","COPY",FACE,{"derivedFrom":makeQuery(id+"F3.opExtrude","CAP_FACE",FACE,{"disambiguationData":[OSD([subQ5,subQ1,subQ6,subQ7,subQ4,subQ3,subQ2,subQ0])],"isStart":false})})}),makeQuery(id+"F8.opExtrude","SWEPT_FACE",FACE,{"disambiguationData":[OSD([sQuery(id+"F7.wireOp",EDGE,"E67")])]})]});}
            var Q5;
            Q5=makeQuery(id+"F8.boolean.opBoolean","INTERSECT",EDGE,{"disambiguationData":[OD(0.0)],"derivedFrom":[makeQuery(id+"F5.opExtrude","SWEPT_FACE",FACE,{"disambiguationData":[OSD([sQuery(id+"F4.wireOp",EDGE,"E30")])]}),makeQuery(id+"F8.opExtrude","SWEPT_FACE",FACE,{"disambiguationData":[OSD([sQuery(id+"F7.wireOp",EDGE,"E67")])]})]});
            fillet(context, id + "F14", {"entities" : qUnion([Q0, Q1, Q2, Q3, Q4, Q5]), "radius" : 3 * mm, "tangentPropagation" : true, "allowEdgeOverflow" : false});
        }
        {
            var Q0;
            Q0=makeQuery(id+"F1.opExtrude","CAP_EDGE",EDGE,{"disambiguationData":[OSD([sQuery(id+"F0.wireOp",EDGE,"E1.bottom")])],"isStart":false});
            fillet(context, id + "F15", {"entities" : qUnion([Q0]), "radius" : 2 * mm, "tangentPropagation" : true, "allowEdgeOverflow" : false});
        }
        {
            var Q0;
            {var subQ0=sQuery(id+"F0.wireOp",EDGE,"E22.filletArc");var subQ1=sQuery(id+"F0.wireOp",EDGE,"E7");var subQ2=sQuery(id+"F0.wireOp",EDGE,"E6");var subQ3=sQuery(id+"F0.wireOp",EDGE,"E5");var subQ4=sQuery(id+"F0.wireOp",EDGE,"E4");var subQ5=sQuery(id+"F0.wireOp",EDGE,"E1.bottom");var subQ6=sQuery(id+"F0.wireOp",EDGE,"E21.filletArc");var subQ7=sQuery(id+"F0.wireOp",EDGE,"E1.top");var subQ8=sQuery(id+"F0.wireOp",EDGE,"E1.left");var subQ9=sQuery(id+"F0.wireOp",EDGE,"E1.right");var subQ10=sQuery(id+"F0.wireOp",EDGE,"E23.filletArc");var subQ11=sQuery(id+"F0.wireOp",EDGE,"E24.filletArc");Q0=makeQuery(id+"F2.boolean.opBoolean","SPLIT",FACE,{"disambiguationData":[TD([makeQuery(id+"F1.opExtrude","SWEPT_FACE",FACE,{"disambiguationData":[OSD([subQ5])]})])],"derivedFrom":makeQuery(id+"F1.opExtrude","CAP_FACE",FACE,{"disambiguationData":[OSD([subQ5,subQ7,subQ8,subQ9,subQ4,subQ3,subQ2,subQ1,subQ6,subQ0,subQ10,subQ11])],"isStart":true})});}
            var sketch = newSketch(context, id + "F16", { "sketchPlane" : qUnion([Q0])});
            skLineSegment(sketch, "E79", {"start": v(0, 90) * mm, "end": v(0, 120) * mm, "construction": true});
            skLineSegment(sketch, "E80", {"start": v(-33, 90) * mm, "end": v(-15, 108) * mm});
            skLineSegment(sketch, "E81", {"start": v(-15, 108) * mm, "end": v(-15, 120) * mm});
            skLineSegment(sketch, "E82", {"start": v(33, 90) * mm, "end": v(15, 108) * mm});
            skLineSegment(sketch, "E83", {"start": v(15, 108) * mm, "end": v(15, 120) * mm});
            skArc(sketch, "E84", {"start": v(15, 120) * mm, "mid": v(0, 135) * mm, "end": v(-15, 120) * mm});
            skCircle(sketch, "E85", {"center": v(0, 120) * mm, "radius": 6 * mm});
            skLineSegment(sketch, "E86", {"start": v(-80, 0) * mm, "end": v(80, 0) * mm, "construction": true});
            skLineSegment(sketch, "E87.MirrorCS", {"start": v(-33, -90) * mm, "end": v(-15, -108) * mm});
            skLineSegment(sketch, "E88.MirrorCS", {"start": v(33, -90) * mm, "end": v(15, -108) * mm});
            skLineSegment(sketch, "E89.MirrorCS", {"start": v(0, -90) * mm, "end": v(0, -120) * mm, "construction": true});
            skCircle(sketch, "E90.MirrorC", {"center": v(0, -120) * mm, "radius": 6 * mm});
            skArc(sketch, "E91.MirrorCS", {"start": v(15, -120) * mm, "mid": v(0, -135) * mm, "end": v(-15, -120) * mm});
            skLineSegment(sketch, "E92.MirrorCS", {"start": v(-15, -108) * mm, "end": v(-15, -120) * mm});
            skLineSegment(sketch, "E93.MirrorCS", {"start": v(15, -108) * mm, "end": v(15, -120) * mm});
            skSolve(sketch);
        }
        {
            var Q0;
            {var subQ0=sQuery(id+"F16.wireOp",EDGE,"E87.MirrorCS");Q0=makeQuery(id+"F16.imprint","IMPRINT",FACE,{"disambiguationData":[TD([[makeQuery(id+"F16.imprint","IMPRINT",EDGE,{"derivedFrom":subQ0}),1.0]])]});}
            var Q1;
            {var subQ1=sQuery(id+"F16.wireOp",EDGE,"E80");Q1=makeQuery(id+"F16.imprint","IMPRINT",FACE,{"disambiguationData":[TD([[makeQuery(id+"F16.imprint","IMPRINT",EDGE,{"derivedFrom":subQ1}),-1.0]])]});}
            var Q2;
            Q2=makeQuery(id+"F16.imprint","IMPRINT",FACE,{"disambiguationData":[TD([[makeQuery(id+"F16.imprint","IMPRINT",EDGE,{"derivedFrom":makeQuery(id+"F1.opExtrude","CAP_EDGE",EDGE,{"disambiguationData":[OSD([sQuery(id+"F0.wireOp",EDGE,"E1.left")])],"isStart":true})}),-1.0]])]});
            var Q3;
            Q3=makeQuery(id+"F2.opExtrude","CAP_FACE",FACE,{"disambiguationData":[OSD([sQuery(id+"F0.wireOp",EDGE,"E12"),sQuery(id+"F0.wireOp",EDGE,"E13"),sQuery(id+"F0.wireOp",EDGE,"E14"),sQuery(id+"F0.wireOp",EDGE,"E15"),sQuery(id+"F0.wireOp",EDGE,"E17.filletArc"),sQuery(id+"F0.wireOp",EDGE,"E18.filletArc"),sQuery(id+"F0.wireOp",EDGE,"E19.filletArc"),sQuery(id+"F0.wireOp",EDGE,"E20.filletArc"),sQuery(id+"F0.wireOp",EDGE,"E25.0"),sQuery(id+"F0.wireOp",EDGE,"E25.1"),sQuery(id+"F0.wireOp",EDGE,"E25.2"),sQuery(id+"F0.wireOp",EDGE,"E25.3"),sQuery(id+"F0.wireOp",EDGE,"E25.4"),sQuery(id+"F0.wireOp",EDGE,"E25.5"),sQuery(id+"F0.wireOp",EDGE,"E25.6"),sQuery(id+"F0.wireOp",EDGE,"E25.7")])],"isStart":false});
            extrude(context, id + "F17", {"entities" : qUnion([Q0, Q1, Q2]), "endBound" : BoundingType.UP_TO_SURFACE, "endBoundEntityFace" : qUnion([Q3]), "depth" : 25 * mm});
        }
    });
